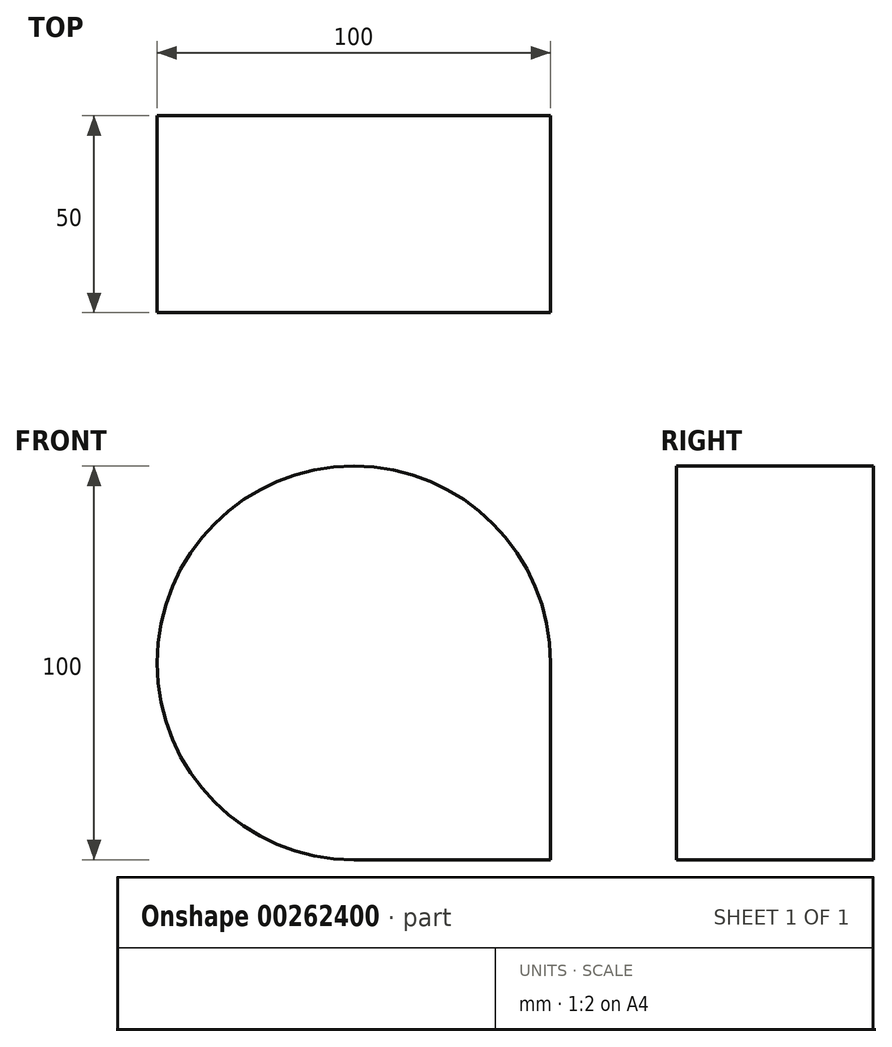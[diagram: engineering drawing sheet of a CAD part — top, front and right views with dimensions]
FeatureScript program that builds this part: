
annotation { "Feature Type Name" : "Feature", "Feature Type Description" : "" }
export const myFeature = defineFeature(function(context is Context, id is Id, definition is map)
    precondition{}
    {
        {
            var Q0;
            Q0=qCreatedBy(makeId("Top.planeOp"),FACE);
            var sketch = newSketch(context, id + "F0", { "sketchPlane" : qUnion([Q0])});
            skLineSegment(sketch, "E0", {"start": v(-38.27, 23.25) * mm, "end": v(11.73, 23.25) * mm});
            skLineSegment(sketch, "E1", {"start": v(11.73, 23.25) * mm, "end": v(11.73, -26.75) * mm});
            skLineSegment(sketch, "E2", {"start": v(11.73, -26.75) * mm, "end": v(-38.27, -26.75) * mm});
            skLineSegment(sketch, "E3", {"start": v(-38.27, -26.75) * mm, "end": v(-38.27, 23.25) * mm});
            skSolve(sketch);
        }
        {
            var Q0;
            Q0=makeQuery(id+"F0.imprint","IMPRINT",FACE,{"disambiguationData":[TD([[makeQuery(id+"F0.imprint","IMPRINT",EDGE,{"derivedFrom":sQuery(id+"F0.wireOp",EDGE,"E0")}),-1.0]])]});
            extrude(context, id + "F1", {"entities" : qUnion([Q0]), "endBound" : BoundingType.SYMMETRIC, "depth" : 50 * mm});
        }
        {
            var Q0;
            Q0=makeQuery(id+"F1.opExtrude","CAP_FACE",FACE,{"disambiguationData":[OSD([sQuery(id+"F0.wireOp",EDGE,"E0"),sQuery(id+"F0.wireOp",EDGE,"E1"),sQuery(id+"F0.wireOp",EDGE,"E2"),sQuery(id+"F0.wireOp",EDGE,"E3")])],"isStart":false});
            var Q1;
            Q1=makeQuery(id+"F1.opExtrude","CAP_EDGE",EDGE,{"disambiguationData":[OSD([sQuery(id+"F0.wireOp",EDGE,"E3")])],"isStart":false});
            revolve(context, id + "F2", {"operationType" : NewBodyOperationType.ADD, "entities" : qUnion([Q0]), "axis" : qUnion([Q1]), "revolveType" : RevolveType.FULL});
        }
    });
